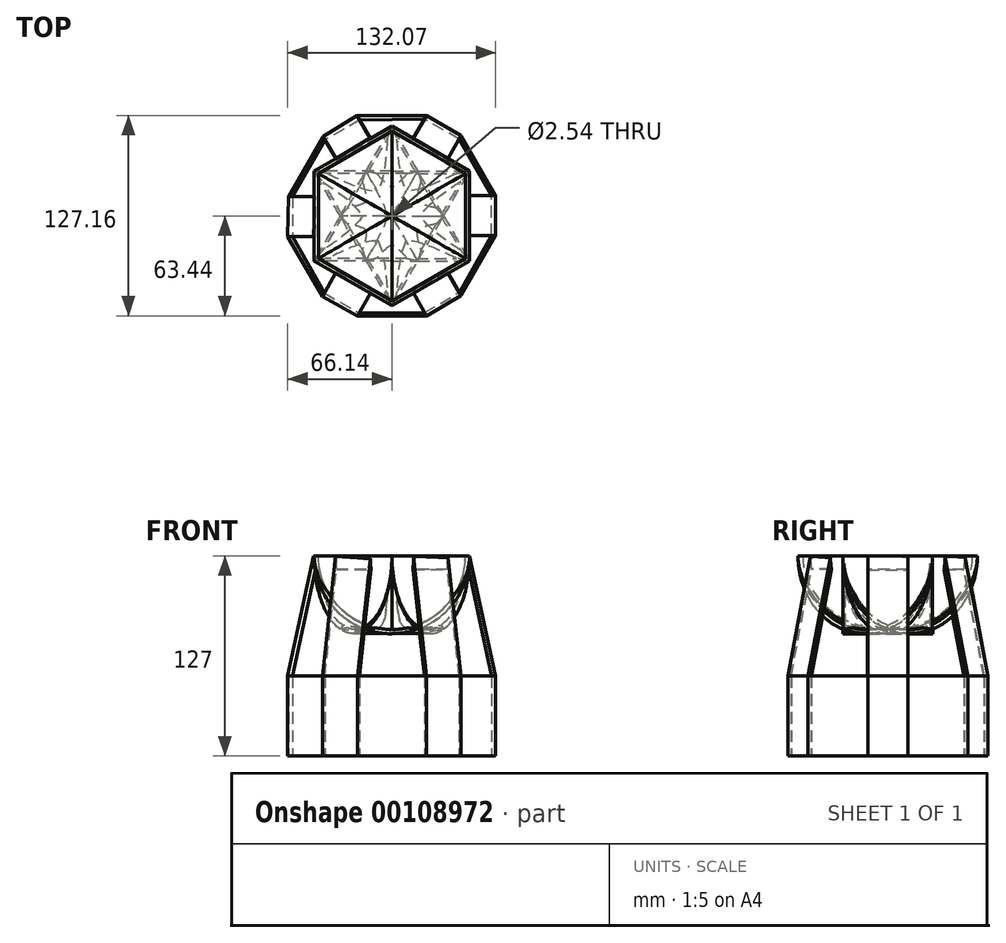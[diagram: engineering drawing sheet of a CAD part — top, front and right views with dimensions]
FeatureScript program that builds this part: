
annotation { "Feature Type Name" : "Feature", "Feature Type Description" : "" }
export const myFeature = defineFeature(function(context is Context, id is Id, definition is map)
    precondition{}
    {
        {
            var Q0;
            Q0=qCreatedBy(makeId("Top.planeOp"),FACE);
            var sketch = newSketch(context, id + "F0", { "sketchPlane" : qUnion([Q0])});
            skLineSegment(sketch, "E0", {"start": v(-65.78, 37.83) * mm, "end": v(-65.78, 12.43) * mm});
            skLineSegment(sketch, "E1", {"start": v(-66.14, -38.37) * mm, "end": v(-66.14, -12.97) * mm});
            skLineSegment(sketch, "E2", {"start": v(-65.78, 12.43) * mm, "end": v(-63.24, 12.43) * mm});
            skLineSegment(sketch, "E3", {"start": v(-63.24, 12.43) * mm, "end": v(-63.24, -12.97) * mm});
            skLineSegment(sketch, "E4", {"start": v(-63.24, -12.97) * mm, "end": v(-66.14, -12.97) * mm});
            skLineSegment(sketch, "E5", {"start": v(-65.78, 37.83) * mm, "end": v(-43.77, 50.5) * mm});
            skLineSegment(sketch, "E6", {"start": v(-0.1, 76.39) * mm, "end": v(-22.12, 63.72) * mm});
            skLineSegment(sketch, "E7", {"start": v(-43.77, 50.5) * mm, "end": v(-42.5, 48.3) * mm});
            skLineSegment(sketch, "E8", {"start": v(-42.5, 48.3) * mm, "end": v(-20.48, 60.96) * mm});
            skLineSegment(sketch, "E9", {"start": v(-20.48, 60.96) * mm, "end": v(-22.12, 63.72) * mm});
            skLineSegment(sketch, "E10", {"start": v(-0.1, 76.39) * mm, "end": v(21.9, 63.69) * mm});
            skLineSegment(sketch, "E11", {"start": v(21.9, 63.69) * mm, "end": v(20.66, 61.54) * mm});
            skLineSegment(sketch, "E12", {"start": v(20.66, 61.54) * mm, "end": v(42.65, 48.84) * mm});
            skLineSegment(sketch, "E13", {"start": v(42.65, 48.84) * mm, "end": v(43.92, 51.04) * mm});
            skLineSegment(sketch, "E14", {"start": v(43.92, 51.04) * mm, "end": v(65.92, 38.34) * mm});
            skLineSegment(sketch, "E15", {"start": v(65.92, 38.34) * mm, "end": v(65.92, 12.94) * mm});
            skLineSegment(sketch, "E16", {"start": v(65.92, 12.94) * mm, "end": v(63.39, 12.94) * mm});
            skLineSegment(sketch, "E17", {"start": v(63.39, 12.94) * mm, "end": v(63.39, -12.46) * mm});
            skLineSegment(sketch, "E18", {"start": v(63.39, -12.46) * mm, "end": v(65.93, -12.46) * mm});
            skLineSegment(sketch, "E19", {"start": v(65.93, -12.46) * mm, "end": v(65.93, -37.86) * mm});
            skLineSegment(sketch, "E20", {"start": v(65.93, -37.86) * mm, "end": v(43.93, -50.56) * mm});
            skLineSegment(sketch, "E21", {"start": v(43.93, -50.56) * mm, "end": v(42.77, -48.54) * mm});
            skLineSegment(sketch, "E22", {"start": v(42.77, -48.54) * mm, "end": v(20.77, -61.24) * mm});
            skLineSegment(sketch, "E23", {"start": v(20.77, -61.24) * mm, "end": v(22.04, -63.44) * mm});
            skLineSegment(sketch, "E24", {"start": v(22.04, -63.44) * mm, "end": v(0.04, -76.14) * mm});
            skLineSegment(sketch, "E25", {"start": v(0.04, -76.14) * mm, "end": v(-21.95, -63.44) * mm});
            skLineSegment(sketch, "E26", {"start": v(-21.95, -63.44) * mm, "end": v(-20.88, -61.57) * mm});
            skLineSegment(sketch, "E27", {"start": v(-20.88, -61.57) * mm, "end": v(-42.87, -48.87) * mm});
            skLineSegment(sketch, "E28", {"start": v(-42.87, -48.87) * mm, "end": v(-44.14, -51.07) * mm});
            skLineSegment(sketch, "E29", {"start": v(-44.14, -51.07) * mm, "end": v(-66.14, -38.37) * mm});
            skSolve(sketch);
        }
        {
            var Q0;
            Q0=qCreatedBy(makeId("Top.planeOp"),FACE);
            var sketch = newSketch(context, id + "F1", { "sketchPlane" : qUnion([Q0])});
            skLineSegment(sketch, "E30.0.0", {"start": v(-43.77, 50.5) * mm, "end": v(-65.78, 37.83) * mm, "construction": true});
            skLineSegment(sketch, "E30.0.1", {"start": v(-65.78, 37.83) * mm, "end": v(-65.78, 12.43) * mm, "construction": true});
            skLineSegment(sketch, "E30.0.2", {"start": v(-65.78, 12.43) * mm, "end": v(-63.24, 12.43) * mm, "construction": true});
            skLineSegment(sketch, "E30.0.3", {"start": v(-63.24, 12.43) * mm, "end": v(-63.24, -12.97) * mm, "construction": true});
            skLineSegment(sketch, "E30.0.4", {"start": v(-63.24, -12.97) * mm, "end": v(-66.14, -12.97) * mm, "construction": true});
            skLineSegment(sketch, "E30.0.5", {"start": v(-66.14, -12.97) * mm, "end": v(-66.14, -38.37) * mm, "construction": true});
            skLineSegment(sketch, "E30.0.6", {"start": v(-66.14, -38.37) * mm, "end": v(-44.14, -51.07) * mm, "construction": true});
            skLineSegment(sketch, "E30.0.7", {"start": v(-44.14, -51.07) * mm, "end": v(-42.87, -48.87) * mm, "construction": true});
            skLineSegment(sketch, "E30.0.8", {"start": v(-42.87, -48.87) * mm, "end": v(-20.88, -61.57) * mm, "construction": true});
            skLineSegment(sketch, "E30.0.9", {"start": v(-20.88, -61.57) * mm, "end": v(-21.95, -63.44) * mm, "construction": true});
            skLineSegment(sketch, "E30.0.10", {"start": v(-21.95, -63.44) * mm, "end": v(0.04, -76.14) * mm, "construction": true});
            skLineSegment(sketch, "E30.0.11", {"start": v(0.04, -76.14) * mm, "end": v(22.04, -63.44) * mm, "construction": true});
            skLineSegment(sketch, "E30.0.12", {"start": v(22.04, -63.44) * mm, "end": v(20.77, -61.24) * mm, "construction": true});
            skLineSegment(sketch, "E30.0.13", {"start": v(20.77, -61.24) * mm, "end": v(42.77, -48.54) * mm, "construction": true});
            skLineSegment(sketch, "E30.0.14", {"start": v(42.77, -48.54) * mm, "end": v(43.93, -50.56) * mm, "construction": true});
            skLineSegment(sketch, "E30.0.15", {"start": v(43.93, -50.56) * mm, "end": v(65.93, -37.86) * mm, "construction": true});
            skLineSegment(sketch, "E30.0.16", {"start": v(65.93, -37.86) * mm, "end": v(65.93, -12.46) * mm, "construction": true});
            skLineSegment(sketch, "E30.0.17", {"start": v(65.93, -12.46) * mm, "end": v(63.39, -12.46) * mm, "construction": true});
            skLineSegment(sketch, "E30.0.18", {"start": v(63.39, -12.46) * mm, "end": v(63.39, 12.94) * mm, "construction": true});
            skLineSegment(sketch, "E30.0.19", {"start": v(63.39, 12.94) * mm, "end": v(65.92, 12.94) * mm, "construction": true});
            skLineSegment(sketch, "E30.0.20", {"start": v(65.92, 12.94) * mm, "end": v(65.92, 38.34) * mm, "construction": true});
            skLineSegment(sketch, "E30.0.21", {"start": v(65.92, 38.34) * mm, "end": v(43.92, 51.04) * mm, "construction": true});
            skLineSegment(sketch, "E30.0.22", {"start": v(43.92, 51.04) * mm, "end": v(42.65, 48.84) * mm, "construction": true});
            skLineSegment(sketch, "E30.0.23", {"start": v(42.65, 48.84) * mm, "end": v(20.66, 61.54) * mm, "construction": true});
            skLineSegment(sketch, "E30.0.24", {"start": v(20.66, 61.54) * mm, "end": v(21.9, 63.69) * mm, "construction": true});
            skLineSegment(sketch, "E30.0.25", {"start": v(21.9, 63.69) * mm, "end": v(-0.1, 76.39) * mm, "construction": true});
            skLineSegment(sketch, "E30.0.26", {"start": v(-0.1, 76.39) * mm, "end": v(-22.12, 63.72) * mm, "construction": true});
            skLineSegment(sketch, "E30.0.27", {"start": v(-22.12, 63.72) * mm, "end": v(-20.48, 60.96) * mm, "construction": true});
            skLineSegment(sketch, "E30.0.28", {"start": v(-20.48, 60.96) * mm, "end": v(-42.5, 48.3) * mm, "construction": true});
            skLineSegment(sketch, "E30.0.29", {"start": v(-42.5, 48.3) * mm, "end": v(-43.77, 50.5) * mm, "construction": true});
            skLineSegment(sketch, "E31", {"start": v(-22.12, 63.72) * mm, "end": v(21.9, 63.69) * mm});
            skLineSegment(sketch, "E32", {"start": v(-43.77, 50.5) * mm, "end": v(-65.78, 12.43) * mm});
            skLineSegment(sketch, "E33", {"start": v(-66.14, -12.97) * mm, "end": v(-44.14, -51.07) * mm});
            skLineSegment(sketch, "E34", {"start": v(-21.95, -63.44) * mm, "end": v(22.04, -63.44) * mm});
            skLineSegment(sketch, "E35", {"start": v(43.93, -50.56) * mm, "end": v(65.93, -12.46) * mm});
            skLineSegment(sketch, "E36", {"start": v(65.92, 12.94) * mm, "end": v(43.92, 51.04) * mm});
            skLineSegment(sketch, "E37", {"start": v(-66.14, -12.97) * mm, "end": v(-65.78, 12.43) * mm});
            skLineSegment(sketch, "E38", {"start": v(-43.77, 50.5) * mm, "end": v(-22.12, 63.72) * mm});
            skLineSegment(sketch, "E39", {"start": v(21.9, 63.69) * mm, "end": v(43.92, 51.04) * mm});
            skLineSegment(sketch, "E40", {"start": v(65.92, 12.94) * mm, "end": v(65.93, -12.46) * mm});
            skLineSegment(sketch, "E41", {"start": v(22.04, -63.44) * mm, "end": v(43.93, -50.56) * mm});
            skLineSegment(sketch, "E42", {"start": v(-21.95, -63.44) * mm, "end": v(-44.14, -51.07) * mm});
            skLineSegment(sketch, "E43", {"start": v(-63.24, 12.43) * mm, "end": v(-42.5, 48.3) * mm});
            skLineSegment(sketch, "E44", {"start": v(-42.5, 48.3) * mm, "end": v(-20.48, 60.96) * mm});
            skLineSegment(sketch, "E45", {"start": v(-20.48, 60.96) * mm, "end": v(20.66, 61.54) * mm});
            skLineSegment(sketch, "E46", {"start": v(20.66, 61.54) * mm, "end": v(42.65, 48.84) * mm});
            skLineSegment(sketch, "E47", {"start": v(63.39, 12.94) * mm, "end": v(63.39, -12.46) * mm});
            skLineSegment(sketch, "E48", {"start": v(42.65, 48.84) * mm, "end": v(63.39, 12.94) * mm});
            skLineSegment(sketch, "E49", {"start": v(63.39, -12.46) * mm, "end": v(42.77, -48.54) * mm});
            skLineSegment(sketch, "E50", {"start": v(42.77, -48.54) * mm, "end": v(20.77, -61.24) * mm});
            skLineSegment(sketch, "E51", {"start": v(-63.24, 12.43) * mm, "end": v(-63.24, -12.97) * mm});
            skLineSegment(sketch, "E52", {"start": v(-63.24, -12.97) * mm, "end": v(-42.87, -48.87) * mm});
            skLineSegment(sketch, "E53", {"start": v(-42.87, -48.87) * mm, "end": v(-20.88, -61.57) * mm});
            skLineSegment(sketch, "E54", {"start": v(-20.88, -61.57) * mm, "end": v(20.77, -61.24) * mm});
            skSolve(sketch);
        }
        {
            var Q0;
            Q0 = qSketchRegion(id + "F1", true);
            extrude(context, id + "F2", {"entities" : qUnion([Q0]), "depth" : 50.8 * mm});
        }
        {
            var Q0;
            Q0=qCreatedBy(makeId("Top.planeOp"),FACE);
            var sketch = newSketch(context, id + "F3", { "sketchPlane" : qUnion([Q0])});
            skLineSegment(sketch, "E55.0.2", {"start": v(-65.78, 12.43) * mm, "end": v(-63.24, 12.43) * mm});
            skLineSegment(sketch, "E55.0.3", {"start": v(-63.24, 12.43) * mm, "end": v(-63.24, -12.97) * mm});
            skLineSegment(sketch, "E55.0.4", {"start": v(-63.24, -12.97) * mm, "end": v(-66.14, -12.97) * mm});
            skLineSegment(sketch, "E55.0.7", {"start": v(-44.14, -51.07) * mm, "end": v(-42.87, -48.87) * mm});
            skLineSegment(sketch, "E55.0.8", {"start": v(-42.87, -48.87) * mm, "end": v(-20.88, -61.57) * mm});
            skLineSegment(sketch, "E55.0.9", {"start": v(-20.88, -61.57) * mm, "end": v(-21.95, -63.44) * mm});
            skLineSegment(sketch, "E55.0.12", {"start": v(22.04, -63.44) * mm, "end": v(20.77, -61.24) * mm});
            skLineSegment(sketch, "E55.0.13", {"start": v(20.77, -61.24) * mm, "end": v(42.77, -48.54) * mm});
            skLineSegment(sketch, "E55.0.14", {"start": v(42.77, -48.54) * mm, "end": v(43.93, -50.56) * mm});
            skLineSegment(sketch, "E55.0.17", {"start": v(65.93, -12.46) * mm, "end": v(63.39, -12.46) * mm});
            skLineSegment(sketch, "E55.0.18", {"start": v(63.39, -12.46) * mm, "end": v(63.39, 12.94) * mm});
            skLineSegment(sketch, "E55.0.19", {"start": v(63.39, 12.94) * mm, "end": v(65.92, 12.94) * mm});
            skLineSegment(sketch, "E55.0.22", {"start": v(43.92, 51.04) * mm, "end": v(42.65, 48.84) * mm});
            skLineSegment(sketch, "E55.0.23", {"start": v(42.65, 48.84) * mm, "end": v(20.66, 61.54) * mm});
            skLineSegment(sketch, "E55.0.24", {"start": v(20.66, 61.54) * mm, "end": v(21.9, 63.69) * mm});
            skLineSegment(sketch, "E55.0.27", {"start": v(-22.12, 63.72) * mm, "end": v(-20.48, 60.96) * mm});
            skLineSegment(sketch, "E55.0.28", {"start": v(-20.48, 60.96) * mm, "end": v(-42.5, 48.3) * mm});
            skLineSegment(sketch, "E55.0.29", {"start": v(-42.5, 48.3) * mm, "end": v(-43.77, 50.5) * mm});
            skLineSegment(sketch, "E56", {"start": v(-65.78, 12.43) * mm, "end": v(-66.14, -12.97) * mm});
            skLineSegment(sketch, "E57", {"start": v(-44.14, -51.07) * mm, "end": v(-21.95, -63.44) * mm});
            skLineSegment(sketch, "E58", {"start": v(22.04, -63.44) * mm, "end": v(43.93, -50.56) * mm});
            skLineSegment(sketch, "E59", {"start": v(65.92, 12.94) * mm, "end": v(65.93, -12.46) * mm});
            skLineSegment(sketch, "E60", {"start": v(43.92, 51.04) * mm, "end": v(21.9, 63.69) * mm});
            skLineSegment(sketch, "E61", {"start": v(-22.12, 63.72) * mm, "end": v(-43.77, 50.5) * mm});
            skSolve(sketch);
        }
        {
            var Q0;
            Q0 = qSketchRegion(id + "F3", true);
            extrude(context, id + "F4", {"entities" : qUnion([Q0]), "operationType" : NewBodyOperationType.ADD, "oppositeDirection" : true, "depth" : 1 / 203.2 * mm});
        }
        {
            var Q0;
            Q0=qCreatedBy(makeId("Top.planeOp"),FACE);
            cPlane(context, id + "F5", {"entities" : qUnion([Q0]), "cplaneType" : CPlaneType.OFFSET, "offset" : 127 * mm, "width" : 152.4 * mm, "height" : 152.4 * mm});
        }
        {
            var Q0;
            Q0=qCreatedBy(id+"F5.planeOp",FACE);
            var sketch = newSketch(context, id + "F6", { "sketchPlane" : qUnion([Q0])});
            skLineSegment(sketch, "E62.0", {"start": v(0, 56.95) * mm, "end": v(49.32, 28.48) * mm, "construction": true});
            skLineSegment(sketch, "E62.1", {"start": v(49.32, 28.48) * mm, "end": v(49.32, -28.48) * mm, "construction": true});
            skLineSegment(sketch, "E62.2", {"start": v(49.32, -28.48) * mm, "end": v(0, -56.95) * mm, "construction": true});
            skLineSegment(sketch, "E62.3", {"start": v(0, -56.95) * mm, "end": v(-49.32, -28.48) * mm, "construction": true});
            skLineSegment(sketch, "E62.4", {"start": v(-49.32, -28.48) * mm, "end": v(-49.32, 28.48) * mm, "construction": true});
            skLineSegment(sketch, "E62.5", {"start": v(-49.32, 28.48) * mm, "end": v(0, 56.95) * mm, "construction": true});
            skLineSegment(sketch, "E63.0", {"start": v(0, 53.98) * mm, "end": v(46.74, 26.99) * mm, "construction": true});
            skLineSegment(sketch, "E63.1", {"start": v(46.74, 26.99) * mm, "end": v(46.74, -26.99) * mm, "construction": true});
            skLineSegment(sketch, "E63.2", {"start": v(46.74, -26.99) * mm, "end": v(0, -53.98) * mm, "construction": true});
            skLineSegment(sketch, "E63.3", {"start": v(0, -53.97) * mm, "end": v(-46.74, -26.99) * mm, "construction": true});
            skLineSegment(sketch, "E63.4", {"start": v(-46.74, -26.99) * mm, "end": v(-46.74, 26.99) * mm, "construction": true});
            skLineSegment(sketch, "E63.5", {"start": v(-46.74, 26.99) * mm, "end": v(0, 53.98) * mm, "construction": true});
            skSolve(sketch);
        }
        {
            var Q0;
            Q0=qCreatedBy(id+"F5.planeOp",FACE);
            var sketch = newSketch(context, id + "F7", { "sketchPlane" : qUnion([Q0])});
            skLineSegment(sketch, "E64.4", {"start": v(-49.5, -28.58) * mm, "end": v(-49.5, 28.57) * mm});
            skLineSegment(sketch, "E65.4", {"start": v(-46.74, -26.99) * mm, "end": v(-46.74, 26.99) * mm});
            skLineSegment(sketch, "E66", {"start": v(-49.5, 28.57) * mm, "end": v(-46.74, 26.99) * mm});
            skLineSegment(sketch, "E67", {"start": v(-49.5, -28.58) * mm, "end": v(-46.74, -26.99) * mm});
            skSolve(sketch);
        }
        {
            var Q0;
            Q0=qCreatedBy(makeId("Right.planeOp"),FACE);
            var sketch = newSketch(context, id + "F8", { "sketchPlane" : qUnion([Q0])});
            skLineSegment(sketch, "E68", {"start": v(0, 0) * mm, "end": v(0, 127) * mm, "construction": true});
            skArc(sketch, "E69", {"start": v(-57.15, 127) * mm, "mid": v(0, 69.85) * mm, "end": v(57.15, 127) * mm, "construction": true});
            skArc(sketch, "E70", {"start": v(-53.98, 127) * mm, "mid": v(0, 73.02) * mm, "end": v(53.98, 127) * mm, "construction": true});
            skSolve(sketch);
        }
        {
            var Q0;
            Q0=qCreatedBy(makeId("Right.planeOp"),FACE);
            var Q1;
            Q1=sQuery(id+"F8.wireOp",EDGE,"E68");
            cPlane(context, id + "F9", {"entities" : qUnion([Q0, Q1]), "cplaneType" : CPlaneType.LINE_ANGLE, "offset" : 25.4 * mm, "angle" : 60 * degree, "width" : 152.4 * mm, "height" : 152.4 * mm});
        }
        {
            var Q0;
            Q0=qCreatedBy(makeId("Right.planeOp"),FACE);
            var Q1;
            Q1=sQuery(id+"F8.wireOp",EDGE,"E68");
            cPlane(context, id + "F10", {"entities" : qUnion([Q0, Q1]), "cplaneType" : CPlaneType.LINE_ANGLE, "offset" : 25.4 * mm, "angle" : 120 * degree, "width" : 152.4 * mm, "height" : 152.4 * mm});
        }
        {
            var Q0;
            Q0=qCreatedBy(id+"F9.planeOp",FACE);
            var sketch = newSketch(context, id + "F11", { "sketchPlane" : qUnion([Q0])});
            skLineSegment(sketch, "E71.0", {"start": v(0, 0) * mm, "end": v(0, 127) * mm, "construction": true});
            skArc(sketch, "E72", {"start": v(57.15, 127) * mm, "mid": v(0, 69.85) * mm, "end": v(-57.15, 127) * mm, "construction": true});
            skArc(sketch, "E73", {"start": v(53.98, 127) * mm, "mid": v(0, 73.02) * mm, "end": v(-53.98, 127) * mm, "construction": true});
            skSolve(sketch);
        }
        {
            var Q0;
            Q0=qCreatedBy(id+"F10.planeOp",FACE);
            var sketch = newSketch(context, id + "F12", { "sketchPlane" : qUnion([Q0])});
            skLineSegment(sketch, "E74.0", {"start": v(0, 0) * mm, "end": v(0, 127) * mm, "construction": true});
            skArc(sketch, "E75", {"start": v(-57.15, 127) * mm, "mid": v(0, 69.85) * mm, "end": v(57.15, 127) * mm, "construction": true});
            skArc(sketch, "E76", {"start": v(-53.98, 127) * mm, "mid": v(0, 73.02) * mm, "end": v(53.98, 127) * mm, "construction": true});
            skSolve(sketch);
        }
        {
            var Q0;
            Q0=qCreatedBy(id+"F5.planeOp",FACE);
            var sketch = newSketch(context, id + "F13", { "sketchPlane" : qUnion([Q0])});
            skLineSegment(sketch, "E77", {"start": v(0, 57.11) * mm, "end": v(0, -57.36) * mm});
            skSolve(sketch);
        }
        {
            var Q0;
            Q0=makeQuery(id+"F7.imprint","IMPRINT",FACE,{"disambiguationData":[TD([[makeQuery(id+"F7.imprint","IMPRINT",EDGE,{"derivedFrom":sQuery(id+"F7.wireOp",EDGE,"E64.4")}),-1.0]])]});
            var Q1;
            Q1=sQuery(id+"F13.wireOp",EDGE,"E77");
            revolve(context, id + "F14", {"entities" : qUnion([Q0]), "axis" : qUnion([Q1]), "revolveType" : RevolveType.ONE_DIRECTION, "angle" : 90 * degree});
        }
        {
            var Q0;
            Q0=qCreatedBy(id+"F5.planeOp",FACE);
            var sketch = newSketch(context, id + "F15", { "sketchPlane" : qUnion([Q0])});
            skLineSegment(sketch, "E78.0", {"start": v(-49.32, 28.48) * mm, "end": v(0, 56.95) * mm});
            skLineSegment(sketch, "E78.1", {"start": v(-46.74, 26.99) * mm, "end": v(0, 53.98) * mm});
            skLineSegment(sketch, "E79", {"start": v(-49.32, 28.48) * mm, "end": v(-46.74, 26.99) * mm});
            skLineSegment(sketch, "E80", {"start": v(0, 53.98) * mm, "end": v(0, 56.95) * mm});
            skLineSegment(sketch, "E81.0", {"start": v(46.74, 26.99) * mm, "end": v(-46.74, -26.99) * mm});
            skSolve(sketch);
        }
        {
            var Q0;
            Q0 = qSketchRegion(id + "F15", true);
            var Q1;
            Q1=sQuery(id+"F15.wireOp",EDGE,"E81.0");
            revolve(context, id + "F16", {"operationType" : NewBodyOperationType.ADD, "entities" : qUnion([Q0]), "axis" : qUnion([Q1]), "revolveType" : RevolveType.ONE_DIRECTION, "angle" : 90 * degree});
        }
        {
            var Q0;
            Q0=qCreatedBy(id+"F5.planeOp",FACE);
            var sketch = newSketch(context, id + "F17", { "sketchPlane" : qUnion([Q0])});
            skLineSegment(sketch, "E82.0", {"start": v(0, 53.98) * mm, "end": v(46.74, 26.99) * mm});
            skLineSegment(sketch, "E82.1", {"start": v(0, 56.95) * mm, "end": v(49.32, 28.48) * mm});
            skLineSegment(sketch, "E83", {"start": v(0, 53.98) * mm, "end": v(0, 56.95) * mm});
            skLineSegment(sketch, "E84", {"start": v(46.74, 26.99) * mm, "end": v(49.32, 28.48) * mm});
            skLineSegment(sketch, "E85.0", {"start": v(-46.74, 26.99) * mm, "end": v(46.74, -26.99) * mm, "construction": true});
            skSolve(sketch);
        }
        {
            var Q0;
            Q0=makeQuery(id+"F17.imprint","IMPRINT",FACE,{"disambiguationData":[TD([[makeQuery(id+"F17.imprint","IMPRINT",EDGE,{"derivedFrom":sQuery(id+"F17.wireOp",EDGE,"E82.0")}),1.0]])]});
            var Q1;
            Q1=sQuery(id+"F17.wireOp",EDGE,"E85.0");
            revolve(context, id + "F18", {"operationType" : NewBodyOperationType.ADD, "entities" : qUnion([Q0]), "axis" : qUnion([Q1]), "revolveType" : RevolveType.ONE_DIRECTION, "oppositeDirection" : true, "angle" : 90 * degree});
        }
        {
            var Q0;
            Q0=qCreatedBy(id+"F5.planeOp",FACE);
            var sketch = newSketch(context, id + "F19", { "sketchPlane" : qUnion([Q0])});
            skLineSegment(sketch, "E86.0", {"start": v(0, -53.97) * mm, "end": v(-46.74, -26.99) * mm});
            skLineSegment(sketch, "E86.1", {"start": v(0, -56.95) * mm, "end": v(-49.32, -28.48) * mm});
            skLineSegment(sketch, "E87", {"start": v(-46.74, -26.99) * mm, "end": v(-49.32, -28.48) * mm});
            skLineSegment(sketch, "E88", {"start": v(0, -56.95) * mm, "end": v(0, -53.97) * mm});
            skSolve(sketch);
        }
        {
            var Q0;
            Q0=makeQuery(id+"F19.imprint","IMPRINT",FACE,{"disambiguationData":[TD([[makeQuery(id+"F19.imprint","IMPRINT",EDGE,{"derivedFrom":sQuery(id+"F19.wireOp",EDGE,"E86.0")}),1.0]])]});
            var Q1;
            Q1=sQuery(id+"F17.wireOp",EDGE,"E85.0");
            revolve(context, id + "F20", {"operationType" : NewBodyOperationType.ADD, "entities" : qUnion([Q0]), "axis" : qUnion([Q1]), "revolveType" : RevolveType.ONE_DIRECTION, "angle" : 90 * degree});
        }
        {
            var Q0;
            Q0=qCreatedBy(id+"F5.planeOp",FACE);
            var sketch = newSketch(context, id + "F21", { "sketchPlane" : qUnion([Q0])});
            skLineSegment(sketch, "E89.0", {"start": v(46.74, 26.99) * mm, "end": v(46.74, -26.99) * mm});
            skLineSegment(sketch, "E89.1", {"start": v(49.32, 28.48) * mm, "end": v(49.32, -28.48) * mm});
            skLineSegment(sketch, "E90", {"start": v(46.74, 26.99) * mm, "end": v(49.32, 28.48) * mm});
            skLineSegment(sketch, "E91", {"start": v(46.74, -26.99) * mm, "end": v(49.32, -28.48) * mm});
            skSolve(sketch);
        }
        {
            var Q0;
            Q0 = qSketchRegion(id + "F21", true);
            var Q1;
            Q1=sQuery(id+"F13.wireOp",EDGE,"E77");
            revolve(context, id + "F22", {"operationType" : NewBodyOperationType.ADD, "entities" : qUnion([Q0]), "axis" : qUnion([Q1]), "revolveType" : RevolveType.ONE_DIRECTION, "oppositeDirection" : true, "angle" : 90 * degree});
        }
        {
            var Q0;
            Q0=qCreatedBy(id+"F5.planeOp",FACE);
            var sketch = newSketch(context, id + "F23", { "sketchPlane" : qUnion([Q0])});
            skLineSegment(sketch, "E92.0", {"start": v(49.32, -28.48) * mm, "end": v(0, -56.95) * mm});
            skLineSegment(sketch, "E92.1", {"start": v(46.74, -26.99) * mm, "end": v(0, -53.98) * mm});
            skLineSegment(sketch, "E93", {"start": v(0, -53.98) * mm, "end": v(0, -56.95) * mm});
            skLineSegment(sketch, "E94", {"start": v(46.74, -26.99) * mm, "end": v(49.32, -28.48) * mm});
            skSolve(sketch);
        }
        {
            var Q0;
            Q0 = qSketchRegion(id + "F23", true);
            var Q1;
            Q1=sQuery(id+"F15.wireOp",EDGE,"E81.0");
            revolve(context, id + "F24", {"operationType" : NewBodyOperationType.ADD, "entities" : qUnion([Q0]), "axis" : qUnion([Q1]), "revolveType" : RevolveType.ONE_DIRECTION, "oppositeDirection" : true, "angle" : 90 * degree});
        }
        {
            var Q0;
            Q0=qCreatedBy(id+"F5.planeOp",FACE);
            cPlane(context, id + "F25", {"entities" : qUnion([Q0]), "cplaneType" : CPlaneType.OFFSET, "offset" : 50.8 * mm, "oppositeDirection" : true, "width" : 152.4 * mm, "height" : 152.4 * mm});
        }
        {
            var Q0;
            Q0=qCreatedBy(id+"F25.planeOp",FACE);
            var sketch = newSketch(context, id + "F26", { "sketchPlane" : qUnion([Q0])});
            skPoint(sketch, "E95", {"position": v(0, 0) * mm});
            skSolve(sketch);
        }
        {
            var Q0;
            Q0=sQuery(id+"F26.wireOp",VERTEX,"E95");
            var Q1;
            Q1=makeQuery(id+"F14.opRevolve","SWEPT_BODY",BODY,{"disambiguationData":[OSD([sQuery(id+"F7.wireOp",EDGE,"E64.4"),sQuery(id+"F7.wireOp",EDGE,"E65.4"),sQuery(id+"F7.wireOp",EDGE,"E66"),sQuery(id+"F7.wireOp",EDGE,"E67")])]});
            hole(context, id + "F27", {"style" : HoleStyle.SIMPLE, "endStyle" : HoleEndStyle.THROUGH, "oppositeDirection" : true, "holeDiameter" : 2.54 * mm, "startFromSketch" : true, "locations" : qUnion([Q0]), "scope" : qUnion([Q1]), "isTappedThrough" : true});
        }
        {
            var Q0;
            Q0=qCreatedBy(makeId("Right.planeOp"),FACE);
            var Q1;
            Q1=sQuery(id+"F12.wireOp",EDGE,"E74.0");
            cPlane(context, id + "F28", {"entities" : qUnion([Q0, Q1]), "cplaneType" : CPlaneType.LINE_ANGLE, "offset" : 25.4 * mm, "angle" : 30 * degree, "width" : 152.4 * mm, "height" : 152.4 * mm});
        }
        {
            var Q0;
            Q0=qCreatedBy(makeId("Top.planeOp"),FACE);
            cPlane(context, id + "F29", {"entities" : qUnion([Q0]), "cplaneType" : CPlaneType.OFFSET, "offset" : 50.8 * mm, "width" : 152.4 * mm, "height" : 152.4 * mm});
        }
        {
            var Q0;
            Q0=qCreatedBy(id+"F29.planeOp",FACE);
            var sketch = newSketch(context, id + "F30", { "sketchPlane" : qUnion([Q0])});
            skLineSegment(sketch, "E96.0", {"start": v(21.9, 63.69) * mm, "end": v(43.92, 51.04) * mm});
            skLineSegment(sketch, "E96.1", {"start": v(20.66, 61.54) * mm, "end": v(42.65, 48.84) * mm});
            skLineSegment(sketch, "E96.2", {"start": v(-43.77, 50.5) * mm, "end": v(-22.12, 63.72) * mm});
            skLineSegment(sketch, "E96.3", {"start": v(-42.5, 48.3) * mm, "end": v(-20.48, 60.96) * mm});
            skLineSegment(sketch, "E96.4", {"start": v(-66.14, -12.97) * mm, "end": v(-65.78, 12.43) * mm});
            skLineSegment(sketch, "E96.5", {"start": v(-63.24, 12.43) * mm, "end": v(-63.24, -12.97) * mm});
            skLineSegment(sketch, "E96.6", {"start": v(-21.95, -63.44) * mm, "end": v(-44.14, -51.07) * mm});
            skLineSegment(sketch, "E96.7", {"start": v(-42.87, -48.87) * mm, "end": v(-20.88, -61.57) * mm});
            skLineSegment(sketch, "E96.8", {"start": v(22.04, -63.44) * mm, "end": v(43.93, -50.56) * mm});
            skLineSegment(sketch, "E96.9", {"start": v(42.77, -48.54) * mm, "end": v(20.77, -61.24) * mm});
            skLineSegment(sketch, "E96.10", {"start": v(65.92, 12.94) * mm, "end": v(65.93, -12.46) * mm});
            skLineSegment(sketch, "E96.11", {"start": v(63.39, 12.94) * mm, "end": v(63.39, -12.46) * mm});
            skLineSegment(sketch, "E97", {"start": v(-43.77, 50.5) * mm, "end": v(-42.5, 48.3) * mm});
            skLineSegment(sketch, "E98", {"start": v(-22.12, 63.72) * mm, "end": v(-20.48, 60.96) * mm});
            skLineSegment(sketch, "E99", {"start": v(21.9, 63.69) * mm, "end": v(20.66, 61.54) * mm});
            skLineSegment(sketch, "E100", {"start": v(42.65, 48.84) * mm, "end": v(43.92, 51.04) * mm});
            skLineSegment(sketch, "E101", {"start": v(63.39, 12.94) * mm, "end": v(65.92, 12.94) * mm});
            skLineSegment(sketch, "E102", {"start": v(63.39, -12.46) * mm, "end": v(65.93, -12.46) * mm});
            skLineSegment(sketch, "E103", {"start": v(43.93, -50.56) * mm, "end": v(42.77, -48.54) * mm});
            skLineSegment(sketch, "E104", {"start": v(22.04, -63.44) * mm, "end": v(20.77, -61.24) * mm});
            skLineSegment(sketch, "E105", {"start": v(-20.88, -61.57) * mm, "end": v(-21.95, -63.44) * mm});
            skLineSegment(sketch, "E106", {"start": v(-42.87, -48.87) * mm, "end": v(-44.14, -51.07) * mm});
            skLineSegment(sketch, "E107", {"start": v(-63.24, -12.97) * mm, "end": v(-66.14, -12.97) * mm});
            skLineSegment(sketch, "E108", {"start": v(-63.24, 12.43) * mm, "end": v(-65.78, 12.43) * mm});
            skSolve(sketch);
        }
        {
            var Q0;
            Q0=qCreatedBy(id+"F28.planeOp",FACE);
            var sketch = newSketch(context, id + "F31", { "sketchPlane" : qUnion([Q0])});
            skLineSegment(sketch, "E109.0", {"start": v(-66.24, 50.8) * mm, "end": v(-44.2, 50.8) * mm});
            skLineSegment(sketch, "E110.0", {"start": v(-49.32, 127) * mm, "end": v(0, 127) * mm});
            skEllipticalArc(sketch, "E111.0", {"construction": true});
            skLineSegment(sketch, "E112.0", {"start": v(-63.08, 50.8) * mm, "end": v(-63.04, 50.8) * mm});
            skLineSegment(sketch, "E113", {"start": v(-46.74, 127) * mm, "end": v(-63.04, 50.8) * mm});
            skLineSegment(sketch, "E114", {"start": v(-49.32, 127) * mm, "end": v(-66.24, 50.8) * mm});
            skLineSegment(sketch, "E115.0", {"start": v(65.75, 50.8) * mm, "end": v(43.75, 50.8) * mm});
            skLineSegment(sketch, "E116", {"start": v(63.41, 50.8) * mm, "end": v(65.86, 50.8) * mm});
            skLineSegment(sketch, "E117", {"start": v(63.41, 50.8) * mm, "end": v(46.74, 127) * mm});
            const initialGuessF31  = {"E111.0": [0, 0.127, 0, 1, 0.053975, 0.04674372116926508, 1.5707963267948966, 4.71238898038469]};
            skSetInitialGuess(sketch, initialGuessF31);
            skSolve(sketch);
        }
        {
            var Q0;
            Q0=makeQuery(id+"F30.imprint","IMPRINT",FACE,{"disambiguationData":[TD([[makeQuery(id+"F30.imprint","IMPRINT",EDGE,{"derivedFrom":sQuery(id+"F30.wireOp",EDGE,"E96.2")}),-1.0]])]});
            var Q1;
            Q1=sQuery(id+"F31.wireOp",EDGE,"E113");
            sweep(context, id + "F32", {"operationType" : NewBodyOperationType.ADD, "profiles" : qUnion([Q0]), "path" : qUnion([Q1])});
        }
        {
            var Q0;
            Q0=qCreatedBy(makeId("Right.planeOp"),FACE);
            var Q1;
            Q1=sQuery(id+"F12.wireOp",EDGE,"E74.0");
            cPlane(context, id + "F33", {"entities" : qUnion([Q0, Q1]), "cplaneType" : CPlaneType.LINE_ANGLE, "offset" : 25.4 * mm, "angle" : 150 * degree, "width" : 152.4 * mm, "height" : 152.4 * mm});
        }
        {
            var Q0;
            Q0=makeQuery(id+"F30.imprint","IMPRINT",FACE,{"disambiguationData":[TD([[makeQuery(id+"F30.imprint","IMPRINT",EDGE,{"derivedFrom":sQuery(id+"F30.wireOp",EDGE,"E96.8")}),1.0]])]});
            var Q1;
            Q1=sQuery(id+"F31.wireOp",EDGE,"E117");
            sweep(context, id + "F34", {"operationType" : NewBodyOperationType.ADD, "profiles" : qUnion([Q0]), "path" : qUnion([Q1])});
        }
        {
            var Q0;
            Q0=qCreatedBy(makeId("Front.planeOp"),FACE);
            var sketch = newSketch(context, id + "F35", { "sketchPlane" : qUnion([Q0])});
            skLineSegment(sketch, "E118.0", {"start": v(-66.14, 50.8) * mm, "end": v(-44.14, 50.8) * mm});
            skLineSegment(sketch, "E119.0", {"start": v(43.93, 50.8) * mm, "end": v(65.93, 50.8) * mm});
            skLineSegment(sketch, "E120", {"start": v(-63.26, 50.8) * mm, "end": v(-65.72, 50.8) * mm});
            skEllipticalArc(sketch, "E121.0", {"construction": true});
            skLineSegment(sketch, "E122", {"start": v(-63.26, 50.8) * mm, "end": v(-46.74, 127) * mm});
            skLineSegment(sketch, "E123", {"start": v(63.38, 50.8) * mm, "end": v(60.04, 50.8) * mm});
            skLineSegment(sketch, "E124", {"start": v(46.74, 127) * mm, "end": v(63.38, 50.8) * mm});
            const initialGuessF35  = {"E121.0": [0, 0.127, 0, -1, 0.053975, 0.04674372116926509, 4.71238898038469, 1.5707963267948966]};
            skSetInitialGuess(sketch, initialGuessF35);
            skSolve(sketch);
        }
        {
            var Q0;
            Q0=makeQuery(id+"F30.imprint","IMPRINT",FACE,{"disambiguationData":[TD([[makeQuery(id+"F30.imprint","IMPRINT",EDGE,{"derivedFrom":sQuery(id+"F30.wireOp",EDGE,"E96.4")}),-1.0]])]});
            var Q1;
            Q1=sQuery(id+"F35.wireOp",EDGE,"E122");
            sweep(context, id + "F36", {"operationType" : NewBodyOperationType.ADD, "profiles" : qUnion([Q0]), "path" : qUnion([Q1])});
        }
        {
            var Q0;
            Q0=makeQuery(id+"F30.imprint","IMPRINT",FACE,{"disambiguationData":[TD([[makeQuery(id+"F30.imprint","IMPRINT",EDGE,{"derivedFrom":sQuery(id+"F30.wireOp",EDGE,"E96.10")}),-1.0]])]});
            var Q1;
            Q1=sQuery(id+"F35.wireOp",EDGE,"E124");
            sweep(context, id + "F37", {"operationType" : NewBodyOperationType.ADD, "profiles" : qUnion([Q0]), "path" : qUnion([Q1])});
        }
        {
            var Q0;
            Q0=qCreatedBy(id+"F33.planeOp",FACE);
            var sketch = newSketch(context, id + "F38", { "sketchPlane" : qUnion([Q0])});
            skLineSegment(sketch, "E125.0", {"start": v(44.12, 50.8) * mm, "end": v(66.1, 50.8) * mm});
            skLineSegment(sketch, "E126.0", {"start": v(-44.3, 50.8) * mm, "end": v(-66.3, 50.8) * mm});
            skEllipticalArc(sketch, "E127.0", {"construction": true});
            skLineSegment(sketch, "E128", {"start": v(63.66, 50.8) * mm, "end": v(66.1, 50.8) * mm});
            skLineSegment(sketch, "E129", {"start": v(-63.75, 50.8) * mm, "end": v(-65.16, 50.8) * mm});
            skLineSegment(sketch, "E130", {"start": v(46.74, 127) * mm, "end": v(63.66, 50.8) * mm});
            skLineSegment(sketch, "E131", {"start": v(-46.74, 127) * mm, "end": v(-63.75, 50.8) * mm});
            const initialGuessF38  = {"E127.0": [0, 0.127, 0, 1, 0.053975, 0.046743721169265076, 1.5707963267948966, 4.71238898038469]};
            skSetInitialGuess(sketch, initialGuessF38);
            skSolve(sketch);
        }
        {
            var Q0;
            Q0=makeQuery(id+"F30.imprint","IMPRINT",FACE,{"disambiguationData":[TD([[makeQuery(id+"F30.imprint","IMPRINT",EDGE,{"derivedFrom":sQuery(id+"F30.wireOp",EDGE,"E96.0")}),-1.0]])]});
            var Q1;
            Q1=sQuery(id+"F38.wireOp",EDGE,"E130");
            sweep(context, id + "F39", {"operationType" : NewBodyOperationType.ADD, "profiles" : qUnion([Q0]), "path" : qUnion([Q1])});
        }
        {
            var Q0;
            Q0=makeQuery(id+"F30.imprint","IMPRINT",FACE,{"disambiguationData":[TD([[makeQuery(id+"F30.imprint","IMPRINT",EDGE,{"derivedFrom":sQuery(id+"F30.wireOp",EDGE,"E96.6")}),-1.0]])]});
            var Q1;
            Q1=sQuery(id+"F38.wireOp",EDGE,"E131");
            sweep(context, id + "F40", {"operationType" : NewBodyOperationType.ADD, "profiles" : qUnion([Q0]), "path" : qUnion([Q1])});
        }
    });
